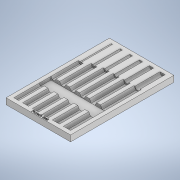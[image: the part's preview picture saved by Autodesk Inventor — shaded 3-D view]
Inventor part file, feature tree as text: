
AUTODESK INVENTOR PART (.ipt)
format: ipt  version: 2020.2 (Build 242310000, 310)  size: 1,036,288 bytes
history: native  units: in
note: dims shown in document units (in); Inventor stores cm internally (conversion verified against a paired STEP export)
features: extrude x12, sketch x12
ambient origin geometry x8: Origin, YZ Plane, XZ Plane, XY Plane, X Axis, Y Axis, Z Axis, Center Point
bodies: Body1 (feature_tree)
feature tree (24):
  extrude  "Extrusion3"  Depth=0.395in
  extrude  "Extrusion4"  Depth=0.25in
  extrude  "5_16_punch"  Depth=0.25in
  extrude  "1_4_punch"  Depth=0.25in
  extrude  "3_16_punch"  Depth=0.25in
  extrude  "5_32_punch"  Depth=0.27in
  extrude  "1_8_punch"  Depth=0.1875in
  extrude  "1_16_punch"  Depth=0.25in TaperAngle=0.0deg
  extrude  "Extrusion5"  Depth=0.3325in
  extrude  "Extrusion12"  Depth=0.27in
  extrude  "Extrusion13"  Depth=0.2075in
  extrude  "Name and Version Number"  Depth=0.125in
  sketch  "Sketch3"  dims[d7=0.395in d8=0.395in]
  sketch  "Sketch4"  dims[d13=0.25in d14=0.25in]
  sketch  "Sketch5"  dims[d15=0.335in d16=0.25in]
  sketch  "Sketch6"  dims[d17=0.335in d18=0.25in]
  sketch  "Sketch7"  dims[d19=0.332in d20=0.25in]
  sketch  "Sketch8"  dims[d21=0.25in d22=0.27in]
  sketch  "Sketch9"  dims[d23=0.25in d24=0.1875in]
  sketch  "Sketch11"  dims[d26=0.0in d27=0.25in d28=0.0in]
  sketch  "Sketch12"  dims[d29=0.25in d30=0.0in d31=0.3325in]
  sketch  "Sketch13"  dims[d32=1.6in d33=0.0in d34=0.27in]
  sketch  "Sketch14"  dims[d35=1.6in d36=0.0in d37=0.2075in]
  sketch  "Sketch15"  dims[d38=1.6in d39=0.0in d40=0.1763in d41=1.6in d42=0.0in d44=0.145in d45=1.75in d46=0.0in d47=0.0825in d48=2.0in d49=0.0in d50=0.75in d51=2.0in d52=0.2in d53=0.0in d54=0.125in d55=0.125in d56=0.0in d57=0.125in d58=0.0in]
